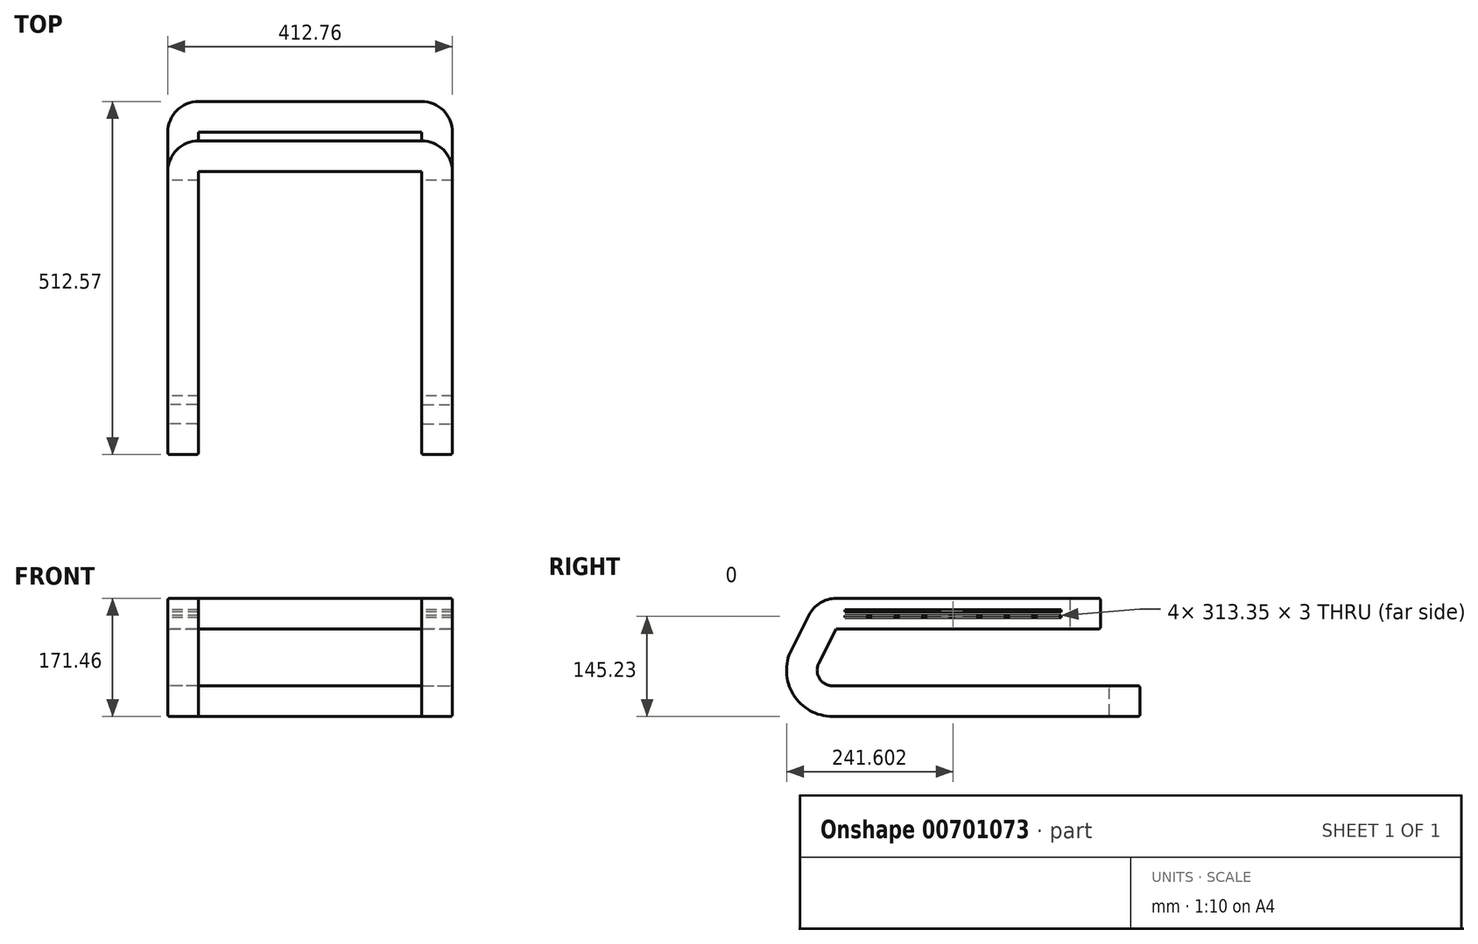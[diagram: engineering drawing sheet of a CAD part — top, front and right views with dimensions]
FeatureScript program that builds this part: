
annotation { "Feature Type Name" : "Feature", "Feature Type Description" : "" }
export const myFeature = defineFeature(function(context is Context, id is Id, definition is map)
    precondition{}
    {
        {
            var Q0;
            Q0=qCreatedBy(makeId("Right.planeOp"),FACE);
            var sketch = newSketch(context, id + "F0", { "sketchPlane" : qUnion([Q0])});
            skLineSegment(sketch, "E0", {"start": v(0, 0) * mm, "end": v(-296.67, 0) * mm});
            skLineSegment(sketch, "E1", {"start": v(-336.35, 64.48) * mm, "end": v(-310.96, 114.79) * mm});
            skLineSegment(sketch, "E2", {"start": v(-291.12, 127) * mm, "end": v(-57.15, 127) * mm});
            skPoint(sketch, "E3.visualSharp", {"position": v(-368.9, 0) * mm});
            skArc(sketch, "E3.filletArc", {"start": v(-336.35, 64.48) * mm, "mid": v(-334.53, 21.15) * mm, "end": v(-296.67, 0) * mm});
            skPoint(sketch, "E4.visualSharp", {"position": v(-304.8, 127) * mm});
            skArc(sketch, "E4.filletArc", {"start": v(-291.12, 127) * mm, "mid": v(-302.77, 123.7) * mm, "end": v(-310.96, 114.79) * mm});
            skLineSegment(sketch, "E5", {"start": v(-341.12, 0) * mm, "end": v(-341.12, 127) * mm, "construction": true});
            skSolve(sketch);
        }
        {
            var Q0;
            Q0=qCreatedBy(makeId("Top.planeOp"),FACE);
            var sketch = newSketch(context, id + "F1", { "sketchPlane" : qUnion([Q0])});
            skLineSegment(sketch, "E6", {"start": v(0, 0) * mm, "end": v(0, 104.78) * mm});
            skLineSegment(sketch, "E7", {"start": v(22.23, 127) * mm, "end": v(184.15, 127) * mm});
            skPoint(sketch, "E8.visualSharp", {"position": v(0, 127) * mm});
            skArc(sketch, "E8.filletArc", {"start": v(22.23, 127) * mm, "mid": v(6.5, 120.5) * mm, "end": v(0, 104.78) * mm});
            skSolve(sketch);
        }
        {
            var Q0;
            Q0=qCreatedBy(makeId("Top.planeOp"),FACE);
            var Q1;
            Q1=sQuery(id+"F0.wireOp",VERTEX,"E2.end");
            cPlane(context, id + "F2", {"entities" : qUnion([Q0, Q1]), "cplaneType" : CPlaneType.PLANE_POINT, "offset" : 25 * mm, "width" : 150 * mm, "height" : 150 * mm});
        }
        {
            var Q0;
            Q0=qCreatedBy(id+"F2.planeOp",FACE);
            var sketch = newSketch(context, id + "F3", { "sketchPlane" : qUnion([Q0])});
            skLineSegment(sketch, "E9.0", {"start": v(0, -291.12) * mm, "end": v(0, -57.15) * mm, "construction": true});
            skLineSegment(sketch, "E10.0", {"start": v(22.23, 127) * mm, "end": v(184.15, 127) * mm, "construction": true});
            skLineSegment(sketch, "E11", {"start": v(22.22, 69.85) * mm, "end": v(184.15, 69.85) * mm});
            skLineSegment(sketch, "E12", {"start": v(184.15, 69.85) * mm, "end": v(184.15, 127) * mm, "construction": true});
            skLineSegment(sketch, "E13", {"start": v(0, 47.62) * mm, "end": v(0, -57.15) * mm});
            skPoint(sketch, "E14.visualSharp", {"position": v(0, 69.85) * mm});
            skArc(sketch, "E14.filletArc", {"start": v(22.22, 69.85) * mm, "mid": v(6.5, 63.34) * mm, "end": v(0, 47.62) * mm});
            skSolve(sketch);
        }
        {
            var Q0;
            Q0=qCreatedBy(makeId("Front.planeOp"),FACE);
            var sketch = newSketch(context, id + "F4", { "sketchPlane" : qUnion([Q0])});
            skLineSegment(sketch, "E15.bottom", {"start": v(19.73, -22.22) * mm, "end": v(-19.72, -22.23) * mm});
            skLineSegment(sketch, "E15.top", {"start": v(19.73, 22.23) * mm, "end": v(-19.72, 22.23) * mm});
            skLineSegment(sketch, "E15.left", {"start": v(22.23, -19.72) * mm, "end": v(22.23, 19.73) * mm});
            skLineSegment(sketch, "E15.right", {"start": v(-22.22, -19.73) * mm, "end": v(-22.22, 19.73) * mm});
            skPoint(sketch, "E15.middle", {"position": v(0, 0) * mm});
            skPoint(sketch, "E16.visualSharp", {"position": v(-22.23, 22.23) * mm});
            skArc(sketch, "E16.filletArc", {"start": v(-19.72, 22.23) * mm, "mid": v(-21.5, 21.5) * mm, "end": v(-22.22, 19.73) * mm});
            skPoint(sketch, "E17.visualSharp", {"position": v(22.23, 22.23) * mm});
            skArc(sketch, "E17.filletArc", {"start": v(22.23, 19.73) * mm, "mid": v(21.5, 21.5) * mm, "end": v(19.73, 22.23) * mm});
            skPoint(sketch, "E18.visualSharp", {"position": v(22.23, -22.22) * mm});
            skArc(sketch, "E18.filletArc", {"start": v(19.73, -22.22) * mm, "mid": v(21.5, -21.5) * mm, "end": v(22.23, -19.72) * mm});
            skPoint(sketch, "E19.visualSharp", {"position": v(-22.22, -22.23) * mm});
            skArc(sketch, "E19.filletArc", {"start": v(-22.22, -19.73) * mm, "mid": v(-21.5, -21.5) * mm, "end": v(-19.72, -22.23) * mm});
            skLineSegment(sketch, "E20", {"start": v(-22.23, 22.23) * mm, "end": v(-22.23, 19.73) * mm, "construction": true});
            skLineSegment(sketch, "E21", {"start": v(-19.72, 22.23) * mm, "end": v(-22.23, 22.23) * mm, "construction": true});
            skLineSegment(sketch, "E22", {"start": v(22.23, 22.23) * mm, "end": v(19.73, 22.23) * mm, "construction": true});
            skLineSegment(sketch, "E23", {"start": v(22.23, 22.23) * mm, "end": v(22.23, 19.73) * mm, "construction": true});
            skLineSegment(sketch, "E24", {"start": v(22.23, -19.72) * mm, "end": v(22.23, -22.23) * mm, "construction": true});
            skLineSegment(sketch, "E25", {"start": v(22.23, -22.22) * mm, "end": v(19.73, -22.22) * mm, "construction": true});
            skLineSegment(sketch, "E26", {"start": v(-19.72, -22.23) * mm, "end": v(-22.22, -22.23) * mm, "construction": true});
            skLineSegment(sketch, "E27", {"start": v(-22.22, -19.73) * mm, "end": v(-22.22, -22.23) * mm, "construction": true});
            skSolve(sketch);
        }
        {
            var Q0;
            Q0 = qSketchRegion(id + "F4", true);
            var Q1;
            Q1 = qConstructionFilter(qBodyType(qCreatedBy(id + "F0" ,EDGE), BodyType.WIRE), ConstructionObject.NO);
            var Q2;
            Q2 = qConstructionFilter(qBodyType(qCreatedBy(id + "F1" ,EDGE), BodyType.WIRE), ConstructionObject.NO);
            var Q3;
            Q3 = qConstructionFilter(qBodyType(qCreatedBy(id + "F3" ,EDGE), BodyType.WIRE), ConstructionObject.NO);
            sweep(context, id + "F5", {"profiles" : qUnion([Q0]), "path" : qUnion([Q1, Q2, Q3])});
        }
        {
            var Q0;
            Q0=makeQuery(id+"F5.opSweep","SWEPT_BODY",BODY,{"disambiguationData":[OSD([sQuery(id+"F4.wireOp",EDGE,"E15.bottom"),sQuery(id+"F4.wireOp",EDGE,"E15.top"),sQuery(id+"F4.wireOp",EDGE,"E15.left"),sQuery(id+"F4.wireOp",EDGE,"E15.right"),sQuery(id+"F4.wireOp",EDGE,"E16.filletArc"),sQuery(id+"F4.wireOp",EDGE,"E17.filletArc"),sQuery(id+"F4.wireOp",EDGE,"E18.filletArc"),sQuery(id+"F4.wireOp",EDGE,"E19.filletArc"),sQuery(id+"F1.wireOp",EDGE,"E7")])]});
            var Q1;
            Q1=makeQuery(id+"F5.opSweep","CAP_FACE",FACE,{"disambiguationData":[OSD([sQuery(id+"F4.wireOp",EDGE,"E15.bottom"),sQuery(id+"F4.wireOp",EDGE,"E15.top"),sQuery(id+"F4.wireOp",EDGE,"E15.left"),sQuery(id+"F4.wireOp",EDGE,"E15.right"),sQuery(id+"F4.wireOp",EDGE,"E16.filletArc"),sQuery(id+"F4.wireOp",EDGE,"E17.filletArc"),sQuery(id+"F4.wireOp",EDGE,"E18.filletArc"),sQuery(id+"F4.wireOp",EDGE,"E19.filletArc"),sQuery(id+"F1.wireOp",VERTEX,"E7.end")])],"isStart":true});
            mirror(context, id + "F6", {"operationType" : NewBodyOperationType.ADD, "entities" : qUnion([Q0]), "mirrorPlane" : qUnion([Q1])});
        }
        {
            var Q0;
            Q0=makeQuery(id+"F5.opSweep","SWEPT_FACE",FACE,{"disambiguationData":[OSD([sQuery(id+"F1.wireOp",EDGE,"E6"),sQuery(id+"F4.wireOp",EDGE,"E15.right")])]});
            var sketch = newSketch(context, id + "F7", { "sketchPlane" : qUnion([Q0])});
            skLineSegment(sketch, "E28.bottom", {"start": v(-47.62, 146.72) * mm, "end": v(291.12, 146.72) * mm, "construction": true});
            skLineSegment(sketch, "E28.top", {"start": v(-47.62, 107.28) * mm, "end": v(291.12, 107.28) * mm, "construction": true});
            skLineSegment(sketch, "E28.left", {"start": v(-47.62, 146.73) * mm, "end": v(-47.62, 107.27) * mm, "construction": true});
            skLineSegment(sketch, "E28.right", {"start": v(291.12, 146.73) * mm, "end": v(291.12, 107.28) * mm, "construction": true});
            skLineSegment(sketch, "E29", {"start": v(-47.62, 127) * mm, "end": v(291.12, 127) * mm, "construction": true});
            skLineSegment(sketch, "E30", {"start": v(121.75, 146.73) * mm, "end": v(121.75, 107.28) * mm, "construction": true});
            skLineSegment(sketch, "E31.bottom", {"start": v(-34.92, 124.5) * mm, "end": v(278.42, 124.5) * mm});
            skLineSegment(sketch, "E31.top", {"start": v(-34.92, 121.5) * mm, "end": v(278.42, 121.5) * mm});
            skLineSegment(sketch, "E31.left", {"start": v(-34.92, 124.5) * mm, "end": v(-34.92, 121.5) * mm});
            skLineSegment(sketch, "E31.right", {"start": v(278.42, 124.5) * mm, "end": v(278.42, 121.5) * mm});
            skLineSegment(sketch, "E32.MirrorCS", {"start": v(-34.92, 129.5) * mm, "end": v(278.42, 129.5) * mm});
            skLineSegment(sketch, "E33.MirrorCS", {"start": v(-34.92, 129.5) * mm, "end": v(-34.92, 132.5) * mm});
            skLineSegment(sketch, "E34.MirrorCS", {"start": v(-34.92, 132.5) * mm, "end": v(278.42, 132.5) * mm});
            skLineSegment(sketch, "E35.MirrorCS", {"start": v(278.42, 129.5) * mm, "end": v(278.42, 132.5) * mm});
            skSolve(sketch);
        }
        {
            var Q0;
            Q0 = qSketchRegion(id + "F7", true);
            extrude(context, id + "F8", {"entities" : qUnion([Q0]), "operationType" : NewBodyOperationType.REMOVE, "endBound" : BoundingType.THROUGH_ALL, "oppositeDirection" : true, "depth" : 25 * mm, "offsetDistance" : 25 * mm, "hasSecondDirection" : true, "secondDirectionBound" : SecondDirectionBoundingType.THROUGH_ALL, "secondDirectionOppositeDirection" : false, "secondDirectionDepth" : 25 * mm});
        }
    });
